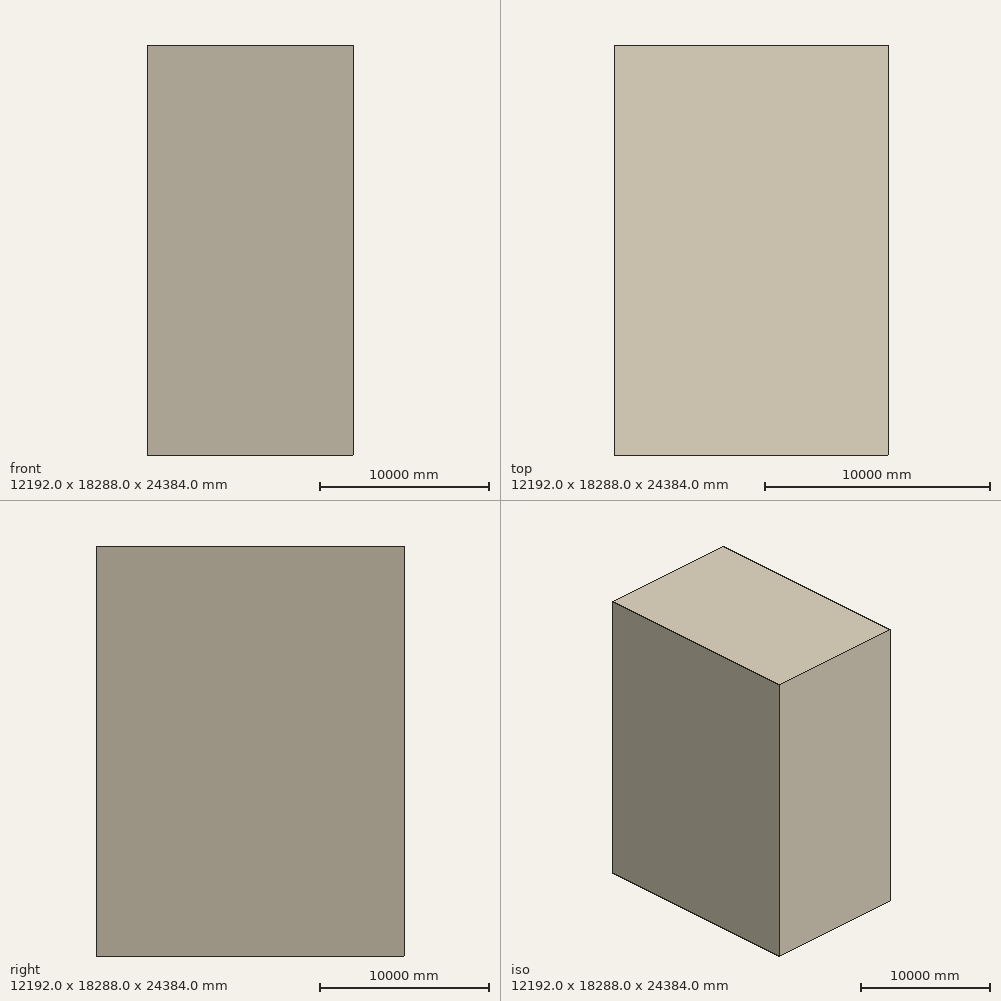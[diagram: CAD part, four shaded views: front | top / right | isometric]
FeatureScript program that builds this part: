
annotation { "Feature Type Name" : "Feature", "Feature Type Description" : "" }
export const myFeature = defineFeature(function(context is Context, id is Id, definition is map)
    precondition{}
    {
        {
            var Q0;
            Q0=qCreatedBy(makeId("Top.planeOp"),FACE);
            var sketch = newSketch(context, id + "F0", { "sketchPlane" : qUnion([Q0])});
            skLineSegment(sketch, "E0.bottom", {"start": v(0, 0) * mm, "end": v(12192, 0) * mm});
            skLineSegment(sketch, "E0.top", {"start": v(0, 18288) * mm, "end": v(12192, 18288) * mm});
            skLineSegment(sketch, "E0.left", {"start": v(0, 0) * mm, "end": v(0, 18288) * mm});
            skLineSegment(sketch, "E0.right", {"start": v(12192, 0) * mm, "end": v(12192, 18288) * mm});
            skSolve(sketch);
        }
        {
            var Q0;
            Q0=makeQuery(id+"F0.imprint","IMPRINT",FACE,{"disambiguationData":[TD([[makeQuery(id+"F0.imprint","IMPRINT",EDGE,{"derivedFrom":sQuery(id+"F0.wireOp",EDGE,"E0.bottom")}),1.0]])]});
            extrude(context, id + "F1", {"entities" : qUnion([Q0]), "depth" : 24384 * mm, "offsetDistance" : 30.48 * mm});
        }
    });
